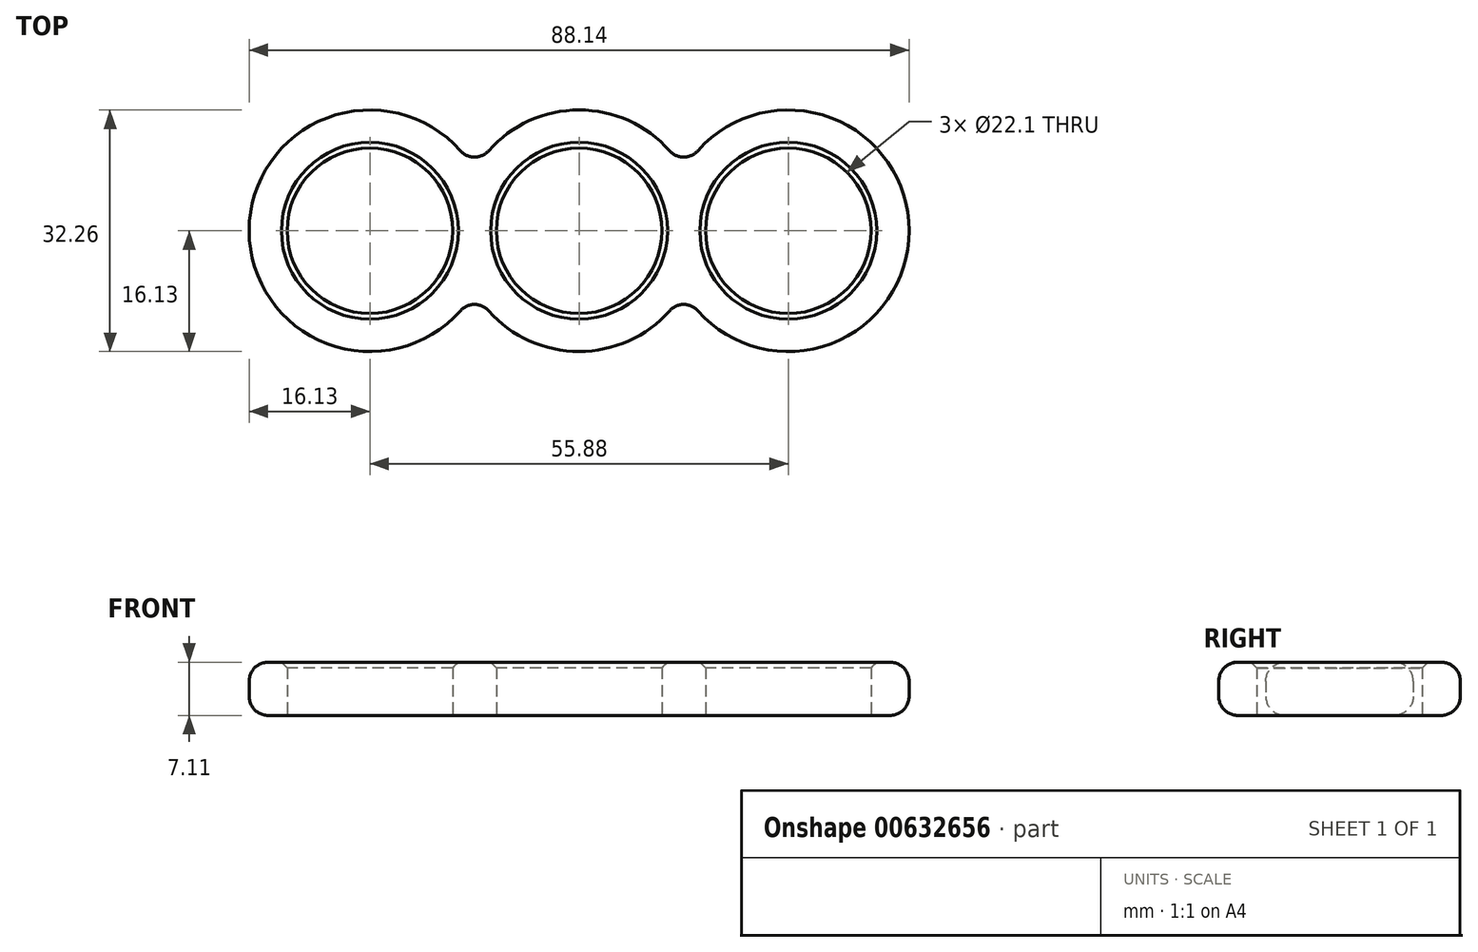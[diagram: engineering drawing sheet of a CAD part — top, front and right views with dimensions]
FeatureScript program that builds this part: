
annotation { "Feature Type Name" : "Feature", "Feature Type Description" : "" }
export const myFeature = defineFeature(function(context is Context, id is Id, definition is map)
    precondition{}
    {
        {
            var Q0;
            Q0=qCreatedBy(makeId("Top.planeOp"),FACE);
            var sketch = newSketch(context, id + "F0", { "sketchPlane" : qUnion([Q0])});
            skCircle(sketch, "E0", {"center": v(0, 0) * mm, "radius": 11.05 * mm});
            skCircle(sketch, "E1", {"center": v(27.94, 0) * mm, "radius": 11.05 * mm});
            skCircle(sketch, "E2.MirrorC", {"center": v(-27.94, 0) * mm, "radius": 11.05 * mm});
            skArc(sketch, "E3.0", {"start": v(-12.07, -10.7) * mm, "mid": v(0, -16.13) * mm, "end": v(12.07, -10.7) * mm});
            skArc(sketch, "E4.0", {"start": v(15.87, -10.7) * mm, "mid": v(44.07, 0) * mm, "end": v(15.87, 10.7) * mm});
            skArc(sketch, "E5.0", {"start": v(-15.87, -10.7) * mm, "mid": v(-44.07, 0) * mm, "end": v(-15.87, 10.7) * mm});
            skArc(sketch, "E6.trimOffspring", {"start": v(12.07, 10.7) * mm, "mid": v(0, 16.13) * mm, "end": v(-12.07, 10.7) * mm});
            skPoint(sketch, "E7.visualSharp", {"position": v(-13.97, 8.06) * mm});
            skArc(sketch, "E7.filletArc", {"start": v(-15.87, 10.7) * mm, "mid": v(-13.97, 9.84) * mm, "end": v(-12.07, 10.7) * mm});
            skPoint(sketch, "E8.visualSharp", {"position": v(13.97, 8.06) * mm});
            skArc(sketch, "E8.filletArc", {"start": v(12.07, 10.7) * mm, "mid": v(13.97, 9.84) * mm, "end": v(15.87, 10.7) * mm});
            skPoint(sketch, "E9.visualSharp", {"position": v(13.97, -8.06) * mm});
            skArc(sketch, "E9.filletArc", {"start": v(15.87, -10.7) * mm, "mid": v(13.97, -9.84) * mm, "end": v(12.07, -10.7) * mm});
            skPoint(sketch, "E10.visualSharp", {"position": v(-13.97, -8.06) * mm});
            skArc(sketch, "E10.filletArc", {"start": v(-12.07, -10.7) * mm, "mid": v(-13.97, -9.84) * mm, "end": v(-15.87, -10.7) * mm});
            skSolve(sketch);
        }
        {
            var Q0;
            Q0=makeQuery(id+"F0.imprint","IMPRINT",FACE,{"disambiguationData":[TD([[makeQuery(id+"F0.imprint","IMPRINT",EDGE,{"derivedFrom":sQuery(id+"F0.wireOp",EDGE,"E0")}),-1.0]])]});
            extrude(context, id + "F1", {"entities" : qUnion([Q0]), "depth" : 7.11 * mm, "offsetDistance" : 25.4 * mm});
        }
        {
            var Q0;
            Q0=makeQuery(id+"F1.opExtrude","CAP_EDGE",EDGE,{"disambiguationData":[OSD([sQuery(id+"F0.wireOp",EDGE,"E4.0")])],"isStart":false});
            var Q1;
            Q1=makeQuery(id+"F1.opExtrude","CAP_EDGE",EDGE,{"disambiguationData":[OSD([sQuery(id+"F0.wireOp",EDGE,"E4.0")])],"isStart":true});
            fillet(context, id + "F2", {"entities" : qUnion([Q0, Q1]), "radius" : 2.54 * mm, "tangentPropagation" : true, "allowEdgeOverflow" : false});
        }
        {
            var Q0;
            Q0=makeQuery(id+"F1.opExtrude","CAP_EDGE",EDGE,{"disambiguationData":[OSD([sQuery(id+"F0.wireOp",EDGE,"E2.MirrorC")])],"isStart":false});
            var Q1;
            Q1=makeQuery(id+"F1.opExtrude","CAP_EDGE",EDGE,{"disambiguationData":[OSD([sQuery(id+"F0.wireOp",EDGE,"E0")])],"isStart":false});
            var Q2;
            Q2=makeQuery(id+"F1.opExtrude","CAP_EDGE",EDGE,{"disambiguationData":[OSD([sQuery(id+"F0.wireOp",EDGE,"E1")])],"isStart":false});
            chamfer(context, id + "F3", {"entities" : qUnion([Q0, Q1, Q2]), "width" : 0.76 * mm, "tangentPropagation" : true});
        }
    });
